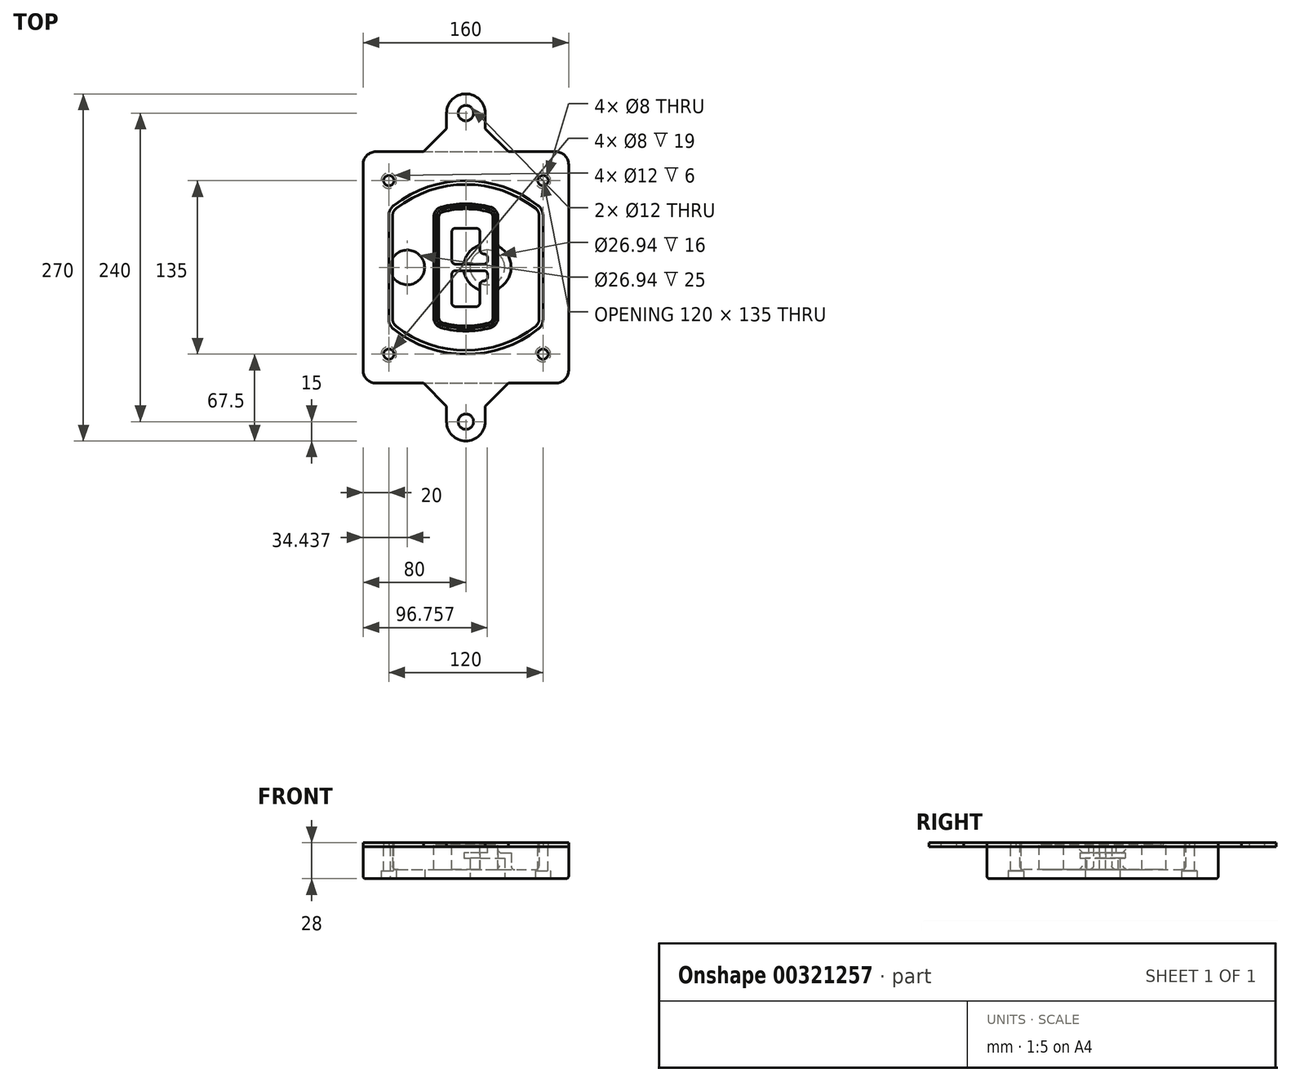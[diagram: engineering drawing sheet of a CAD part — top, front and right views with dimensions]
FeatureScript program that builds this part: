
annotation { "Feature Type Name" : "Feature", "Feature Type Description" : "" }
export const myFeature = defineFeature(function(context is Context, id is Id, definition is map)
    precondition{}
    {
        {
            var Q0;
            Q0=qCreatedBy(makeId("Top.planeOp"),FACE);
            var sketch = newSketch(context, id + "F0", { "sketchPlane" : qUnion([Q0])});
            skPoint(sketch, "E0.rect.middle", {"position": v(0, 0) * mm});
            skLineSegment(sketch, "E1.bottom", {"start": v(-70, -90) * mm, "end": v(70, -90) * mm});
            skLineSegment(sketch, "E1.top", {"start": v(-70, 90) * mm, "end": v(70, 90) * mm});
            skLineSegment(sketch, "E1.left", {"start": v(-80, -80) * mm, "end": v(-80, 80) * mm});
            skLineSegment(sketch, "E1.right", {"start": v(80, -80) * mm, "end": v(80, 80) * mm});
            skLineSegment(sketch, "E2", {"start": v(-80, 90) * mm, "end": v(80, -90) * mm, "construction": true});
            skLineSegment(sketch, "E3", {"start": v(80, 90) * mm, "end": v(-80, -90) * mm, "construction": true});
            skCircle(sketch, "E4", {"center": v(-60, 67.5) * mm, "radius": 4 * mm});
            skCircle(sketch, "E5", {"center": v(60, 67.5) * mm, "radius": 4 * mm});
            skCircle(sketch, "E6", {"center": v(60, -67.5) * mm, "radius": 4 * mm});
            skCircle(sketch, "E7", {"center": v(-60, -67.5) * mm, "radius": 4 * mm});
            skLineSegment(sketch, "E8", {"start": v(-60, 67.5) * mm, "end": v(60, 67.5) * mm, "construction": true});
            skLineSegment(sketch, "E9", {"start": v(60, 67.5) * mm, "end": v(60, -67.5) * mm, "construction": true});
            skLineSegment(sketch, "E10", {"start": v(60, -67.5) * mm, "end": v(-60, -67.5) * mm, "construction": true});
            skLineSegment(sketch, "E11", {"start": v(-60, -67.5) * mm, "end": v(-60, 67.5) * mm, "construction": true});
            skLineSegment(sketch, "E12", {"start": v(-60, 40.3) * mm, "end": v(-60, -40.3) * mm});
            skLineSegment(sketch, "E13", {"start": v(60, 40.3) * mm, "end": v(60, -40.3) * mm});
            skArc(sketch, "E14", {"start": v(56.15, 48.18) * mm, "mid": v(0, 67.5) * mm, "end": v(-56.15, 48.18) * mm});
            skArc(sketch, "E15", {"start": v(-56.15, -48.18) * mm, "mid": v(0, -67.5) * mm, "end": v(56.15, -48.18) * mm});
            skLineSegment(sketch, "E16", {"start": v(-60, 0) * mm, "end": v(60, 0) * mm, "construction": true});
            skPoint(sketch, "E17.visualSharp", {"position": v(-60, -45) * mm});
            skArc(sketch, "E17.filletArc", {"start": v(-60, -40.3) * mm, "mid": v(-58.99, -44.68) * mm, "end": v(-56.15, -48.18) * mm});
            skPoint(sketch, "E18.visualSharp", {"position": v(-60, 45) * mm});
            skArc(sketch, "E18.filletArc", {"start": v(-56.15, 48.18) * mm, "mid": v(-58.99, 44.68) * mm, "end": v(-60, 40.3) * mm});
            skPoint(sketch, "E19.visualSharp", {"position": v(60, 45) * mm});
            skArc(sketch, "E19.filletArc", {"start": v(60, 40.3) * mm, "mid": v(58.99, 44.68) * mm, "end": v(56.15, 48.18) * mm});
            skPoint(sketch, "E20.visualSharp", {"position": v(60, -45) * mm});
            skArc(sketch, "E20.filletArc", {"start": v(56.15, -48.18) * mm, "mid": v(58.99, -44.68) * mm, "end": v(60, -40.3) * mm});
            skPoint(sketch, "E21.visualSharp", {"position": v(-80, 90) * mm});
            skArc(sketch, "E21.filletArc", {"start": v(-70, 90) * mm, "mid": v(-77.07, 87.07) * mm, "end": v(-80, 80) * mm});
            skPoint(sketch, "E22.visualSharp", {"position": v(80, 90) * mm});
            skArc(sketch, "E22.filletArc", {"start": v(80, 80) * mm, "mid": v(77.07, 87.07) * mm, "end": v(70, 90) * mm});
            skPoint(sketch, "E23.visualSharp", {"position": v(80, -90) * mm});
            skArc(sketch, "E23.filletArc", {"start": v(70, -90) * mm, "mid": v(77.07, -87.07) * mm, "end": v(80, -80) * mm});
            skPoint(sketch, "E24.visualSharp", {"position": v(-80, -90) * mm});
            skArc(sketch, "E24.filletArc", {"start": v(-80, -80) * mm, "mid": v(-77.07, -87.07) * mm, "end": v(-70, -90) * mm});
            skArc(sketch, "E25.0", {"start": v(57, 40.3) * mm, "mid": v(56.3, 43.36) * mm, "end": v(54.3, 45.81) * mm});
            skLineSegment(sketch, "E25.1", {"start": v(57, 40.3) * mm, "end": v(57, -40.3) * mm});
            skArc(sketch, "E25.2", {"start": v(54.3, -45.81) * mm, "mid": v(56.3, -43.36) * mm, "end": v(57, -40.3) * mm});
            skArc(sketch, "E25.3", {"start": v(-54.3, -45.81) * mm, "mid": v(0, -64.5) * mm, "end": v(54.3, -45.81) * mm});
            skArc(sketch, "E25.4", {"start": v(-57, -40.3) * mm, "mid": v(-56.3, -43.36) * mm, "end": v(-54.3, -45.81) * mm});
            skArc(sketch, "E25.5", {"start": v(54.3, 45.81) * mm, "mid": v(0, 64.5) * mm, "end": v(-54.3, 45.81) * mm});
            skLineSegment(sketch, "E25.6", {"start": v(-57, 40.3) * mm, "end": v(-57, -40.3) * mm});
            skArc(sketch, "E25.7", {"start": v(-54.3, 45.81) * mm, "mid": v(-56.3, 43.36) * mm, "end": v(-57, 40.3) * mm});
            skArc(sketch, "E26.0", {"start": v(-58.62, 51.33) * mm, "mid": v(-62.58, 46.43) * mm, "end": v(-64, 40.3) * mm});
            skArc(sketch, "E26.1", {"start": v(58.62, 51.33) * mm, "mid": v(0, 71.5) * mm, "end": v(-58.62, 51.33) * mm});
            skArc(sketch, "E26.2", {"start": v(64, 40.3) * mm, "mid": v(62.58, 46.43) * mm, "end": v(58.62, 51.33) * mm});
            skLineSegment(sketch, "E26.3", {"start": v(64, 40.3) * mm, "end": v(64, -40.3) * mm});
            skArc(sketch, "E26.4", {"start": v(58.62, -51.33) * mm, "mid": v(62.58, -46.43) * mm, "end": v(64, -40.3) * mm});
            skLineSegment(sketch, "E26.5", {"start": v(-64, 40.3) * mm, "end": v(-64, -40.3) * mm});
            skArc(sketch, "E26.6", {"start": v(-58.62, -51.33) * mm, "mid": v(0, -71.5) * mm, "end": v(58.62, -51.33) * mm});
            skArc(sketch, "E26.7", {"start": v(-64, -40.3) * mm, "mid": v(-62.58, -46.43) * mm, "end": v(-58.62, -51.33) * mm});
            skSolve(sketch);
        }
        {
            var Q0;
            Q0=makeQuery(id+"F0.imprint","IMPRINT",FACE,{"disambiguationData":[TD([[makeQuery(id+"F0.imprint","IMPRINT",EDGE,{"derivedFrom":sQuery(id+"F0.wireOp",EDGE,"E1.bottom")}),1.0]])]});
            var Q1;
            Q1=makeQuery(id+"F0.imprint","IMPRINT",FACE,{"disambiguationData":[TD([[makeQuery(id+"F0.imprint","IMPRINT",EDGE,{"derivedFrom":sQuery(id+"F0.wireOp",EDGE,"E12")}),1.0]])]});
            var Q2;
            Q2=makeQuery(id+"F0.imprint","IMPRINT",FACE,{"disambiguationData":[TD([[makeQuery(id+"F0.imprint","IMPRINT",EDGE,{"derivedFrom":sQuery(id+"F0.wireOp",EDGE,"E25.0")}),1.0]])]});
            var Q3;
            Q3=makeQuery(id+"F0.imprint","IMPRINT",FACE,{"disambiguationData":[TD([[makeQuery(id+"F0.imprint","IMPRINT",EDGE,{"derivedFrom":sQuery(id+"F0.wireOp",EDGE,"E12")}),-1.0]])]});
            extrude(context, id + "F1", {"entities" : qUnion([Q0, Q1, Q2, Q3]), "oppositeDirection" : true, "depth" : 25 * mm});
        }
        {
            var Q0;
            Q0=makeQuery(id+"F0.imprint","IMPRINT",FACE,{"disambiguationData":[TD([[makeQuery(id+"F0.imprint","IMPRINT",EDGE,{"derivedFrom":sQuery(id+"F0.wireOp",EDGE,"E12")}),1.0]])]});
            extrude(context, id + "F2", {"entities" : qUnion([Q0]), "operationType" : NewBodyOperationType.ADD, "depth" : 3 * mm});
        }
        {
            var Q0;
            Q0=makeQuery(id+"F0.imprint","IMPRINT",FACE,{"disambiguationData":[TD([[makeQuery(id+"F0.imprint","IMPRINT",EDGE,{"derivedFrom":sQuery(id+"F0.wireOp",EDGE,"E25.0")}),1.0]])]});
            extrude(context, id + "F3", {"entities" : qUnion([Q0]), "operationType" : NewBodyOperationType.REMOVE, "oppositeDirection" : true, "depth" : 18 * mm});
        }
        {
            var Q0;
            Q0=makeQuery(id+"F2.opExtrude","CAP_FACE",FACE,{"disambiguationData":[OSD([sQuery(id+"F0.wireOp",EDGE,"E12"),sQuery(id+"F0.wireOp",EDGE,"E13"),sQuery(id+"F0.wireOp",EDGE,"E14"),sQuery(id+"F0.wireOp",EDGE,"E15"),sQuery(id+"F0.wireOp",EDGE,"E17.filletArc"),sQuery(id+"F0.wireOp",EDGE,"E18.filletArc"),sQuery(id+"F0.wireOp",EDGE,"E19.filletArc"),sQuery(id+"F0.wireOp",EDGE,"E20.filletArc"),sQuery(id+"F0.wireOp",EDGE,"E25.0"),sQuery(id+"F0.wireOp",EDGE,"E25.1"),sQuery(id+"F0.wireOp",EDGE,"E25.2"),sQuery(id+"F0.wireOp",EDGE,"E25.3"),sQuery(id+"F0.wireOp",EDGE,"E25.4"),sQuery(id+"F0.wireOp",EDGE,"E25.5"),sQuery(id+"F0.wireOp",EDGE,"E25.6"),sQuery(id+"F0.wireOp",EDGE,"E25.7")])],"isStart":false});
            var sketch = newSketch(context, id + "F4", { "sketchPlane" : qUnion([Q0])});
            skArc(sketch, "E27.0", {"start": v(-19.08, -46.97) * mm, "mid": v(0, -49.5) * mm, "end": v(19.08, -46.97) * mm});
            skArc(sketch, "E28.0", {"start": v(19.08, 46.97) * mm, "mid": v(0, 49.5) * mm, "end": v(-19.08, 46.97) * mm});
            skLineSegment(sketch, "E29", {"start": v(-25, 39.25) * mm, "end": v(-25, -39.25) * mm});
            skLineSegment(sketch, "E30", {"start": v(25, 39.25) * mm, "end": v(25, -39.25) * mm});
            skLineSegment(sketch, "E31", {"start": v(-25, 45.1) * mm, "end": v(25, 45.1) * mm, "construction": true});
            skLineSegment(sketch, "E32", {"start": v(-25, -45.1) * mm, "end": v(25, -45.1) * mm, "construction": true});
            skPoint(sketch, "E33.visualSharp", {"position": v(-25, 45.1) * mm});
            skArc(sketch, "E33.filletArc", {"start": v(-19.08, 46.97) * mm, "mid": v(-23.35, 44.11) * mm, "end": v(-25, 39.25) * mm});
            skPoint(sketch, "E34.visualSharp", {"position": v(25, 45.1) * mm});
            skArc(sketch, "E34.filletArc", {"start": v(25, 39.25) * mm, "mid": v(23.35, 44.11) * mm, "end": v(19.08, 46.97) * mm});
            skPoint(sketch, "E35.visualSharp", {"position": v(25, -45.1) * mm});
            skArc(sketch, "E35.filletArc", {"start": v(19.08, -46.97) * mm, "mid": v(23.35, -44.11) * mm, "end": v(25, -39.25) * mm});
            skPoint(sketch, "E36.visualSharp", {"position": v(-25, -45.1) * mm});
            skArc(sketch, "E36.filletArc", {"start": v(-25, -39.25) * mm, "mid": v(-23.35, -44.11) * mm, "end": v(-19.08, -46.97) * mm});
            skArc(sketch, "E37.0", {"start": v(54.3, 45.81) * mm, "mid": v(0, 64.5) * mm, "end": v(-54.3, 45.81) * mm});
            skArc(sketch, "E37.1", {"start": v(-54.3, 45.81) * mm, "mid": v(-56.3, 43.36) * mm, "end": v(-57, 40.3) * mm});
            skLineSegment(sketch, "E37.2", {"start": v(-57, 40.3) * mm, "end": v(-57, -40.3) * mm});
            skArc(sketch, "E37.3", {"start": v(-57, -40.3) * mm, "mid": v(-56.3, -43.36) * mm, "end": v(-54.3, -45.81) * mm});
            skArc(sketch, "E37.4", {"start": v(-54.3, -45.81) * mm, "mid": v(0, -64.5) * mm, "end": v(54.3, -45.81) * mm});
            skArc(sketch, "E37.5", {"start": v(54.3, -45.81) * mm, "mid": v(56.3, -43.36) * mm, "end": v(57, -40.3) * mm});
            skLineSegment(sketch, "E37.6", {"start": v(57, 40.3) * mm, "end": v(57, -40.3) * mm});
            skArc(sketch, "E37.7", {"start": v(57, 40.3) * mm, "mid": v(56.3, 43.36) * mm, "end": v(54.3, 45.81) * mm});
            skLineSegment(sketch, "E38.0", {"start": v(23, 39.25) * mm, "end": v(23, -39.25) * mm});
            skArc(sketch, "E38.1", {"start": v(18.56, -45.04) * mm, "mid": v(21.76, -42.9) * mm, "end": v(23, -39.25) * mm});
            skArc(sketch, "E38.2", {"start": v(-18.56, -45.04) * mm, "mid": v(0, -47.5) * mm, "end": v(18.56, -45.04) * mm});
            skArc(sketch, "E38.3", {"start": v(-23, -39.25) * mm, "mid": v(-21.76, -42.9) * mm, "end": v(-18.56, -45.04) * mm});
            skLineSegment(sketch, "E38.4", {"start": v(-23, 39.25) * mm, "end": v(-23, -39.25) * mm});
            skArc(sketch, "E38.5", {"start": v(23, 39.25) * mm, "mid": v(21.76, 42.9) * mm, "end": v(18.56, 45.04) * mm});
            skArc(sketch, "E38.6", {"start": v(-18.56, 45.04) * mm, "mid": v(-21.76, 42.9) * mm, "end": v(-23, 39.25) * mm});
            skArc(sketch, "E38.7", {"start": v(18.56, 45.04) * mm, "mid": v(0, 47.5) * mm, "end": v(-18.56, 45.04) * mm});
            skArc(sketch, "E39.0", {"start": v(21, 39.25) * mm, "mid": v(20.18, 41.68) * mm, "end": v(18.04, 43.1) * mm});
            skLineSegment(sketch, "E39.1", {"start": v(21, 39.25) * mm, "end": v(21, -39.25) * mm});
            skArc(sketch, "E39.2", {"start": v(18.04, -43.1) * mm, "mid": v(20.18, -41.68) * mm, "end": v(21, -39.25) * mm});
            skArc(sketch, "E39.3", {"start": v(-18.04, -43.1) * mm, "mid": v(0, -45.5) * mm, "end": v(18.04, -43.1) * mm});
            skArc(sketch, "E39.4", {"start": v(-21, -39.25) * mm, "mid": v(-20.18, -41.68) * mm, "end": v(-18.04, -43.1) * mm});
            skArc(sketch, "E39.5", {"start": v(18.04, 43.1) * mm, "mid": v(0, 45.5) * mm, "end": v(-18.04, 43.1) * mm});
            skLineSegment(sketch, "E39.6", {"start": v(-21, 39.25) * mm, "end": v(-21, -39.25) * mm});
            skArc(sketch, "E39.7", {"start": v(-18.04, 43.1) * mm, "mid": v(-20.18, 41.68) * mm, "end": v(-21, 39.25) * mm});
            skLineSegment(sketch, "E40", {"start": v(-25, 0) * mm, "end": v(25, 0) * mm, "construction": true});
            skLineSegment(sketch, "E41", {"start": v(-11, 5.5) * mm, "end": v(-11, 27.5) * mm});
            skLineSegment(sketch, "E42", {"start": v(-8, 30.5) * mm, "end": v(8, 30.5) * mm});
            skLineSegment(sketch, "E43", {"start": v(11, 27.5) * mm, "end": v(11, 13.5) * mm});
            skLineSegment(sketch, "E44", {"start": v(14, 10.5) * mm, "end": v(14, 10.5) * mm});
            skLineSegment(sketch, "E45", {"start": v(17, 7.5) * mm, "end": v(17, 5.5) * mm});
            skLineSegment(sketch, "E46", {"start": v(14, 2.5) * mm, "end": v(-8, 2.5) * mm});
            skPoint(sketch, "E47.visualSharp", {"position": v(-11, 30.5) * mm});
            skArc(sketch, "E47.filletArc", {"start": v(-8, 30.5) * mm, "mid": v(-10.12, 29.62) * mm, "end": v(-11, 27.5) * mm});
            skPoint(sketch, "E48.visualSharp", {"position": v(11, 30.5) * mm});
            skArc(sketch, "E48.filletArc", {"start": v(11, 27.5) * mm, "mid": v(10.12, 29.62) * mm, "end": v(8, 30.5) * mm});
            skPoint(sketch, "E49.visualSharp", {"position": v(11, 10.5) * mm});
            skArc(sketch, "E49.filletArc", {"start": v(11, 13.5) * mm, "mid": v(11.88, 11.38) * mm, "end": v(14, 10.5) * mm});
            skPoint(sketch, "E50.visualSharp", {"position": v(17, 10.5) * mm});
            skArc(sketch, "E50.filletArc", {"start": v(17, 7.5) * mm, "mid": v(16.12, 9.62) * mm, "end": v(14, 10.5) * mm});
            skPoint(sketch, "E51.visualSharp", {"position": v(17, 2.5) * mm});
            skArc(sketch, "E51.filletArc", {"start": v(14, 2.5) * mm, "mid": v(16.12, 3.38) * mm, "end": v(17, 5.5) * mm});
            skPoint(sketch, "E52.visualSharp", {"position": v(-11, 2.5) * mm});
            skArc(sketch, "E52.filletArc", {"start": v(-11, 5.5) * mm, "mid": v(-10.12, 3.38) * mm, "end": v(-8, 2.5) * mm});
            skLineSegment(sketch, "E53.0.MirrorCS", {"start": v(14, -2.5) * mm, "end": v(-8, -2.5) * mm});
            skArc(sketch, "E54.0.MirrorCS", {"start": v(-11, -5.5) * mm, "mid": v(-10.12, -3.38) * mm, "end": v(-8, -2.5) * mm});
            skLineSegment(sketch, "E55.0.MirrorCS", {"start": v(-11, -5.5) * mm, "end": v(-11, -27.5) * mm});
            skArc(sketch, "E56.0.MirrorCS", {"start": v(-8, -30.5) * mm, "mid": v(-10.12, -29.62) * mm, "end": v(-11, -27.5) * mm});
            skLineSegment(sketch, "E57.0.MirrorCS", {"start": v(-8, -30.5) * mm, "end": v(8, -30.5) * mm});
            skArc(sketch, "E58.0.MirrorCS", {"start": v(11, -27.5) * mm, "mid": v(10.12, -29.62) * mm, "end": v(8, -30.5) * mm});
            skLineSegment(sketch, "E59.0.MirrorCS", {"start": v(11, -27.5) * mm, "end": v(11, -13.5) * mm});
            skArc(sketch, "E60.0.MirrorCS", {"start": v(11, -13.5) * mm, "mid": v(11.88, -11.38) * mm, "end": v(14, -10.5) * mm});
            skArc(sketch, "E61.0.MirrorCS", {"start": v(17, -7.5) * mm, "mid": v(16.12, -9.62) * mm, "end": v(14, -10.5) * mm});
            skLineSegment(sketch, "E62.0.MirrorCS", {"start": v(17, -7.5) * mm, "end": v(17, -5.5) * mm});
            skArc(sketch, "E63.0.MirrorCS", {"start": v(14, -2.5) * mm, "mid": v(16.12, -3.38) * mm, "end": v(17, -5.5) * mm});
            skSolve(sketch);
        }
        {
            var Q0;
            Q0=makeQuery(id+"F4.imprint","IMPRINT",FACE,{"disambiguationData":[TD([[makeQuery(id+"F4.imprint","IMPRINT",EDGE,{"derivedFrom":sQuery(id+"F4.wireOp",EDGE,"E27.0")}),1.0]])]});
            var Q1;
            Q1=makeQuery(id+"F4.imprint","IMPRINT",FACE,{"disambiguationData":[TD([[makeQuery(id+"F4.imprint","IMPRINT",EDGE,{"derivedFrom":sQuery(id+"F4.wireOp",EDGE,"E38.0")}),-1.0]])]});
            var Q2;
            Q2=makeQuery(id+"F4.imprint","IMPRINT",FACE,{"disambiguationData":[TD([[makeQuery(id+"F4.imprint","IMPRINT",EDGE,{"derivedFrom":sQuery(id+"F4.wireOp",EDGE,"E39.0")}),1.0]])]});
            extrude(context, id + "F5", {"entities" : qUnion([Q0, Q1, Q2]), "operationType" : NewBodyOperationType.ADD, "endBound" : BoundingType.UP_TO_NEXT, "oppositeDirection" : true, "depth" : 25 * mm});
        }
        {
            var Q0;
            Q0=makeQuery(id+"F4.imprint","IMPRINT",FACE,{"disambiguationData":[TD([[makeQuery(id+"F4.imprint","IMPRINT",EDGE,{"derivedFrom":sQuery(id+"F4.wireOp",EDGE,"E38.0")}),-1.0]])]});
            extrude(context, id + "F6", {"entities" : qUnion([Q0]), "operationType" : NewBodyOperationType.REMOVE, "oppositeDirection" : true, "depth" : 2 * mm});
        }
        {
            var Q0;
            Q0=makeQuery(id+"F1.opExtrude","CAP_FACE",FACE,{"disambiguationData":[OSD([sQuery(id+"F0.wireOp",EDGE,"E1.bottom"),sQuery(id+"F0.wireOp",EDGE,"E1.top"),sQuery(id+"F0.wireOp",EDGE,"E1.left"),sQuery(id+"F0.wireOp",EDGE,"E1.right"),sQuery(id+"F0.wireOp",EDGE,"E4"),sQuery(id+"F0.wireOp",EDGE,"E5"),sQuery(id+"F0.wireOp",EDGE,"E6"),sQuery(id+"F0.wireOp",EDGE,"E7"),sQuery(id+"F0.wireOp",EDGE,"E21.filletArc"),sQuery(id+"F0.wireOp",EDGE,"E22.filletArc"),sQuery(id+"F0.wireOp",EDGE,"E23.filletArc"),sQuery(id+"F0.wireOp",EDGE,"E24.filletArc")])],"isStart":false});
            var sketch = newSketch(context, id + "F7", { "sketchPlane" : qUnion([Q0])});
            skCircle(sketch, "E64", {"center": v(16.76, 0) * mm, "radius": 13.47 * mm});
            skCircle(sketch, "E65", {"center": v(-45.56, 0) * mm, "radius": 13.47 * mm});
            skLineSegment(sketch, "E66", {"start": v(80, 0) * mm, "end": v(-80, 0) * mm});
            skCircle(sketch, "E67", {"center": v(16.76, 0) * mm, "radius": 18.47 * mm});
            skCircle(sketch, "E68", {"center": v(60, -67.5) * mm, "radius": 6 * mm});
            skCircle(sketch, "E69", {"center": v(-60, -67.5) * mm, "radius": 6 * mm});
            skCircle(sketch, "E70", {"center": v(-60, 67.5) * mm, "radius": 6 * mm});
            skCircle(sketch, "E71", {"center": v(60, 67.5) * mm, "radius": 6 * mm});
            skSolve(sketch);
        }
        {
            var Q0;
            {var subQ1=sQuery(id+"F7.wireOp",EDGE,"E66");var subQ4=sQuery(id+"F7.wireOp",EDGE,"E64");var subQ6=makeQuery(id+"F7.imprint","INTERSECT",VERTEX,{"disambiguationData":[OD(0.0)],"derivedFrom":[subQ4,subQ1]});Q0=makeQuery(id+"F7.imprint","IMPRINT",FACE,{"disambiguationData":[TD([[makeQuery(id+"F7.imprint","IMPRINT",EDGE,{"disambiguationData":[TD([[subQ6,-1.0]])],"derivedFrom":subQ4}),-1.0]])]});}
            var Q1;
            {var subQ0=sQuery(id+"F7.wireOp",EDGE,"E66");var subQ1=sQuery(id+"F7.wireOp",EDGE,"E64");var subQ3=makeQuery(id+"F7.imprint","INTERSECT",VERTEX,{"disambiguationData":[OD(0.0)],"derivedFrom":[subQ1,subQ0]});Q1=makeQuery(id+"F7.imprint","IMPRINT",FACE,{"disambiguationData":[TD([[makeQuery(id+"F7.imprint","IMPRINT",EDGE,{"disambiguationData":[TD([[subQ3,-1.0]])],"derivedFrom":subQ1}),1.0]])]});}
            var Q2;
            {var subQ0=sQuery(id+"F7.wireOp",EDGE,"E66");var subQ1=sQuery(id+"F7.wireOp",EDGE,"E64");var subQ3=makeQuery(id+"F7.imprint","INTERSECT",VERTEX,{"disambiguationData":[OD(0.0)],"derivedFrom":[subQ1,subQ0]});Q2=makeQuery(id+"F7.imprint","IMPRINT",FACE,{"disambiguationData":[TD([[makeQuery(id+"F7.imprint","IMPRINT",EDGE,{"disambiguationData":[TD([[subQ3,1.0]])],"derivedFrom":subQ1}),1.0]])]});}
            var Q3;
            {var subQ1=sQuery(id+"F7.wireOp",EDGE,"E66");var subQ4=sQuery(id+"F7.wireOp",EDGE,"E64");var subQ6=makeQuery(id+"F7.imprint","INTERSECT",VERTEX,{"disambiguationData":[OD(0.0)],"derivedFrom":[subQ4,subQ1]});Q3=makeQuery(id+"F7.imprint","IMPRINT",FACE,{"disambiguationData":[TD([[makeQuery(id+"F7.imprint","IMPRINT",EDGE,{"disambiguationData":[TD([[subQ6,1.0]])],"derivedFrom":subQ4}),-1.0]])]});}
            extrude(context, id + "F8", {"entities" : qUnion([Q0, Q1, Q2, Q3]), "operationType" : NewBodyOperationType.ADD, "oppositeDirection" : true, "depth" : 20 * mm});
        }
        {
            var Q0;
            {var subQ0=sQuery(id+"F7.wireOp",EDGE,"E66");var subQ1=sQuery(id+"F7.wireOp",EDGE,"E64");var subQ3=makeQuery(id+"F7.imprint","INTERSECT",VERTEX,{"disambiguationData":[OD(0.0)],"derivedFrom":[subQ1,subQ0]});Q0=makeQuery(id+"F7.imprint","IMPRINT",FACE,{"disambiguationData":[TD([[makeQuery(id+"F7.imprint","IMPRINT",EDGE,{"disambiguationData":[TD([[subQ3,-1.0]])],"derivedFrom":subQ1}),1.0]])]});}
            var Q1;
            {var subQ0=sQuery(id+"F7.wireOp",EDGE,"E66");var subQ1=sQuery(id+"F7.wireOp",EDGE,"E64");var subQ3=makeQuery(id+"F7.imprint","INTERSECT",VERTEX,{"disambiguationData":[OD(0.0)],"derivedFrom":[subQ1,subQ0]});Q1=makeQuery(id+"F7.imprint","IMPRINT",FACE,{"disambiguationData":[TD([[makeQuery(id+"F7.imprint","IMPRINT",EDGE,{"disambiguationData":[TD([[subQ3,1.0]])],"derivedFrom":subQ1}),1.0]])]});}
            extrude(context, id + "F9", {"entities" : qUnion([Q0, Q1]), "operationType" : NewBodyOperationType.REMOVE, "oppositeDirection" : true, "depth" : 16 * mm});
        }
        {
            var Q0;
            {var subQ0=sQuery(id+"F7.wireOp",EDGE,"E66");var subQ1=sQuery(id+"F7.wireOp",EDGE,"E65");var subQ3=makeQuery(id+"F7.imprint","INTERSECT",VERTEX,{"disambiguationData":[OD(0.0)],"derivedFrom":[subQ1,subQ0]});Q0=makeQuery(id+"F7.imprint","IMPRINT",FACE,{"disambiguationData":[TD([[makeQuery(id+"F7.imprint","IMPRINT",EDGE,{"disambiguationData":[TD([[subQ3,-1.0]])],"derivedFrom":subQ1}),1.0]])]});}
            var Q1;
            {var subQ0=sQuery(id+"F7.wireOp",EDGE,"E66");var subQ1=sQuery(id+"F7.wireOp",EDGE,"E65");var subQ3=makeQuery(id+"F7.imprint","INTERSECT",VERTEX,{"disambiguationData":[OD(0.0)],"derivedFrom":[subQ1,subQ0]});Q1=makeQuery(id+"F7.imprint","IMPRINT",FACE,{"disambiguationData":[TD([[makeQuery(id+"F7.imprint","IMPRINT",EDGE,{"disambiguationData":[TD([[subQ3,1.0]])],"derivedFrom":subQ1}),1.0]])]});}
            extrude(context, id + "F10", {"entities" : qUnion([Q0, Q1]), "operationType" : NewBodyOperationType.REMOVE, "oppositeDirection" : true, "depth" : 25 * mm});
        }
        {
            var Q0;
            Q0=makeQuery(id+"F7.imprint","IMPRINT",FACE,{"disambiguationData":[TD([[makeQuery(id+"F7.imprint","IMPRINT",EDGE,{"derivedFrom":sQuery(id+"F7.wireOp",EDGE,"E68")}),1.0]])]});
            var Q1;
            Q1=makeQuery(id+"F7.imprint","IMPRINT",FACE,{"disambiguationData":[TD([[makeQuery(id+"F7.imprint","IMPRINT",EDGE,{"derivedFrom":makeQuery(id+"F1.opExtrude","CAP_EDGE",EDGE,{"disambiguationData":[OSD([sQuery(id+"F0.wireOp",EDGE,"E5")])],"isStart":false})}),-1.0]])]});
            var Q2;
            Q2=makeQuery(id+"F7.imprint","IMPRINT",FACE,{"disambiguationData":[TD([[makeQuery(id+"F7.imprint","IMPRINT",EDGE,{"derivedFrom":sQuery(id+"F7.wireOp",EDGE,"E69")}),1.0]])]});
            var Q3;
            Q3=makeQuery(id+"F7.imprint","IMPRINT",FACE,{"disambiguationData":[TD([[makeQuery(id+"F7.imprint","IMPRINT",EDGE,{"derivedFrom":makeQuery(id+"F1.opExtrude","CAP_EDGE",EDGE,{"disambiguationData":[OSD([sQuery(id+"F0.wireOp",EDGE,"E4")])],"isStart":false})}),-1.0]])]});
            var Q4;
            Q4=makeQuery(id+"F7.imprint","IMPRINT",FACE,{"disambiguationData":[TD([[makeQuery(id+"F7.imprint","IMPRINT",EDGE,{"derivedFrom":sQuery(id+"F7.wireOp",EDGE,"E70")}),1.0]])]});
            var Q5;
            Q5=makeQuery(id+"F7.imprint","IMPRINT",FACE,{"disambiguationData":[TD([[makeQuery(id+"F7.imprint","IMPRINT",EDGE,{"derivedFrom":makeQuery(id+"F1.opExtrude","CAP_EDGE",EDGE,{"disambiguationData":[OSD([sQuery(id+"F0.wireOp",EDGE,"E7")])],"isStart":false})}),-1.0]])]});
            var Q6;
            Q6=makeQuery(id+"F7.imprint","IMPRINT",FACE,{"disambiguationData":[TD([[makeQuery(id+"F7.imprint","IMPRINT",EDGE,{"derivedFrom":sQuery(id+"F7.wireOp",EDGE,"E71")}),1.0]])]});
            var Q7;
            Q7=makeQuery(id+"F7.imprint","IMPRINT",FACE,{"disambiguationData":[TD([[makeQuery(id+"F7.imprint","IMPRINT",EDGE,{"derivedFrom":makeQuery(id+"F1.opExtrude","CAP_EDGE",EDGE,{"disambiguationData":[OSD([sQuery(id+"F0.wireOp",EDGE,"E6")])],"isStart":false})}),-1.0]])]});
            extrude(context, id + "F11", {"entities" : qUnion([Q0, Q1, Q2, Q3, Q4, Q5, Q6, Q7]), "operationType" : NewBodyOperationType.REMOVE, "oppositeDirection" : true, "depth" : 6 * mm});
        }
        {
            var Q0;
            Q0=makeQuery(id+"F9.boolean.opBoolean","COPY",FACE,{"derivedFrom":makeQuery(id+"F9.opExtrude","CAP_FACE",FACE,{"disambiguationData":[OSD([sQuery(id+"F7.wireOp",EDGE,"E64")])],"isStart":false})});
            var sketch = newSketch(context, id + "F12", { "sketchPlane" : qUnion([Q0])});
            skArc(sketch, "E72.0", {"start": v(11, 17.55) * mm, "mid": v(2.57, 11.82) * mm, "end": v(-1.54, 2.5) * mm});
            skArc(sketch, "E72.1", {"start": v(-1.54, -2.5) * mm, "mid": v(2.57, -11.82) * mm, "end": v(11, -17.55) * mm});
            skLineSegment(sketch, "E73", {"start": v(-1.54, -2.5) * mm, "end": v(14, -2.5) * mm});
            skLineSegment(sketch, "E74.0", {"start": v(14, 2.5) * mm, "end": v(-1.54, 2.5) * mm});
            skArc(sketch, "E74.1", {"start": v(14, 2.5) * mm, "mid": v(16.12, 3.38) * mm, "end": v(17, 5.5) * mm});
            skLineSegment(sketch, "E74.2", {"start": v(17, 7.5) * mm, "end": v(17, 5.5) * mm});
            skArc(sketch, "E74.3", {"start": v(17, 7.5) * mm, "mid": v(16.12, 9.62) * mm, "end": v(14, 10.5) * mm});
            skArc(sketch, "E74.4", {"start": v(11, 13.5) * mm, "mid": v(11.88, 11.38) * mm, "end": v(14, 10.5) * mm});
            skLineSegment(sketch, "E74.5", {"start": v(11, 17.55) * mm, "end": v(11, 13.5) * mm});
            skLineSegment(sketch, "E74.7", {"start": v(14, -2.5) * mm, "end": v(-1.54, -2.5) * mm});
            skArc(sketch, "E74.8", {"start": v(14, -2.5) * mm, "mid": v(16.12, -3.38) * mm, "end": v(17, -5.5) * mm});
            skLineSegment(sketch, "E74.9", {"start": v(17, -7.5) * mm, "end": v(17, -5.5) * mm});
            skArc(sketch, "E74.10", {"start": v(17, -7.5) * mm, "mid": v(16.12, -9.62) * mm, "end": v(14, -10.5) * mm});
            skArc(sketch, "E74.11", {"start": v(11, -13.5) * mm, "mid": v(11.88, -11.38) * mm, "end": v(14, -10.5) * mm});
            skLineSegment(sketch, "E74.12", {"start": v(11, -17.55) * mm, "end": v(11, -13.5) * mm});
            skPoint(sketch, "E75.orphan", {"position": v(11, -27.5) * mm});
            skPoint(sketch, "E76.orphan", {"position": v(-8, -2.5) * mm});
            skPoint(sketch, "E77.orphan", {"position": v(-8, 2.5) * mm});
            skPoint(sketch, "E78.orphan", {"position": v(11, 27.5) * mm});
            skSolve(sketch);
        }
        {
            var Q0;
            {var subQ7=sQuery(id+"F12.wireOp",EDGE,"E72.0");var subQ14=sQuery(id+"F12.wireOp",EDGE,"E72.1");var subQ16=sQuery(id+"F12.wireOp",EDGE,"E74.1");var subQ18=sQuery(id+"F12.wireOp",EDGE,"E74.8");Q0=qUnion([makeQuery(id+"F12.imprint","IMPRINT",FACE,{"disambiguationData":[TD([[makeQuery(id+"F12.imprint","IMPRINT",EDGE,{"derivedFrom":subQ7}),1.0]])]}),makeQuery(id+"F12.imprint","IMPRINT",FACE,{"disambiguationData":[TD([[makeQuery(id+"F12.imprint","IMPRINT",EDGE,{"derivedFrom":subQ14}),1.0]])]}),makeQuery(id+"F12.imprint","IMPRINT",FACE,{"disambiguationData":[TD([[makeQuery(id+"F12.imprint","IMPRINT",EDGE,{"derivedFrom":subQ16}),1.0]])]}),makeQuery(id+"F12.imprint","IMPRINT",FACE,{"disambiguationData":[TD([[makeQuery(id+"F12.imprint","IMPRINT",EDGE,{"derivedFrom":subQ18}),-1.0]])]})]);}
            var Q1;
            Q1=makeQuery(id+"F5.boolean.opBoolean","SPLIT",FACE,{"disambiguationData":[TD([makeQuery(id+"F5.opExtrude","SWEPT_FACE",FACE,{"disambiguationData":[OSD([sQuery(id+"F4.wireOp",EDGE,"E41")])]})])],"derivedFrom":makeQuery(id+"F3.boolean.opBoolean","COPY",FACE,{"derivedFrom":makeQuery(id+"F3.opExtrude","CAP_FACE",FACE,{"disambiguationData":[OSD([sQuery(id+"F0.wireOp",EDGE,"E25.0"),sQuery(id+"F0.wireOp",EDGE,"E25.1"),sQuery(id+"F0.wireOp",EDGE,"E25.2"),sQuery(id+"F0.wireOp",EDGE,"E25.3"),sQuery(id+"F0.wireOp",EDGE,"E25.4"),sQuery(id+"F0.wireOp",EDGE,"E25.5"),sQuery(id+"F0.wireOp",EDGE,"E25.6"),sQuery(id+"F0.wireOp",EDGE,"E25.7")])],"isStart":false})})});
            extrude(context, id + "F13", {"entities" : qUnion([Q0]), "operationType" : NewBodyOperationType.REMOVE, "endBound" : BoundingType.UP_TO_SURFACE, "endBoundEntityFace" : qUnion([Q1]), "depth" : 25 * mm});
        }
        {
            var Q0;
            Q0=makeQuery(id+"F3.boolean.opBoolean","COPY",EDGE,{"derivedFrom":makeQuery(id+"F3.opExtrude","CAP_EDGE",EDGE,{"disambiguationData":[OSD([sQuery(id+"F0.wireOp",EDGE,"E25.6")])],"isStart":false})});
            var Q1;
            Q1=makeQuery(id+"F8.boolean.opBoolean","INTERSECT",EDGE,{"derivedFrom":[makeQuery(id+"F5.opExtrude","SWEPT_FACE",FACE,{"disambiguationData":[OSD([sQuery(id+"F4.wireOp",EDGE,"E30")])]}),makeQuery(id+"F8.opExtrude","CAP_FACE",FACE,{"disambiguationData":[OSD([sQuery(id+"F7.wireOp",EDGE,"E67")])],"isStart":false})]});
            var Q2;
            Q2=makeQuery(id+"F8.boolean.opBoolean","INTERSECT",EDGE,{"disambiguationData":[OD(1.0)],"derivedFrom":[makeQuery(id+"F5.opExtrude","SWEPT_FACE",FACE,{"disambiguationData":[OSD([sQuery(id+"F4.wireOp",EDGE,"E30")])]}),makeQuery(id+"F8.opExtrude","SWEPT_FACE",FACE,{"disambiguationData":[OSD([sQuery(id+"F7.wireOp",EDGE,"E67")])]})]});
            var Q3;
            {var subQ0=sQuery(id+"F4.wireOp",EDGE,"E30");Q3=makeQuery(id+"F8.boolean.opBoolean","SPLIT",EDGE,{"disambiguationData":[TD([makeQuery(id+"F5.opExtrude","SWEPT_FACE",FACE,{"disambiguationData":[OSD([sQuery(id+"F4.wireOp",EDGE,"E35.filletArc")])]})])],"derivedFrom":makeQuery(id+"F5.opExtrude","CAP_EDGE",EDGE,{"disambiguationData":[OSD([subQ0])],"isStart":false})});}
            var Q4;
            {var subQ0=sQuery(id+"F0.wireOp",EDGE,"E25.7");var subQ1=sQuery(id+"F0.wireOp",EDGE,"E25.1");var subQ2=sQuery(id+"F0.wireOp",EDGE,"E25.6");var subQ3=sQuery(id+"F0.wireOp",EDGE,"E25.5");var subQ4=sQuery(id+"F0.wireOp",EDGE,"E25.4");var subQ5=sQuery(id+"F0.wireOp",EDGE,"E25.0");var subQ6=sQuery(id+"F0.wireOp",EDGE,"E25.2");var subQ7=sQuery(id+"F0.wireOp",EDGE,"E25.3");Q4=makeQuery(id+"F8.boolean.opBoolean","INTERSECT",EDGE,{"derivedFrom":[makeQuery(id+"F5.boolean.opBoolean","SPLIT",FACE,{"disambiguationData":[TD([makeQuery(id+"F2.opExtrude","SWEPT_FACE",FACE,{"disambiguationData":[OSD([subQ5])]})])],"derivedFrom":makeQuery(id+"F3.boolean.opBoolean","COPY",FACE,{"derivedFrom":makeQuery(id+"F3.opExtrude","CAP_FACE",FACE,{"disambiguationData":[OSD([subQ5,subQ1,subQ6,subQ7,subQ4,subQ3,subQ2,subQ0])],"isStart":false})})}),makeQuery(id+"F8.opExtrude","SWEPT_FACE",FACE,{"disambiguationData":[OSD([sQuery(id+"F7.wireOp",EDGE,"E67")])]})]});}
            var Q5;
            Q5=makeQuery(id+"F8.boolean.opBoolean","INTERSECT",EDGE,{"disambiguationData":[OD(0.0)],"derivedFrom":[makeQuery(id+"F5.opExtrude","SWEPT_FACE",FACE,{"disambiguationData":[OSD([sQuery(id+"F4.wireOp",EDGE,"E30")])]}),makeQuery(id+"F8.opExtrude","SWEPT_FACE",FACE,{"disambiguationData":[OSD([sQuery(id+"F7.wireOp",EDGE,"E67")])]})]});
            fillet(context, id + "F14", {"entities" : qUnion([Q0, Q1, Q2, Q3, Q4, Q5]), "radius" : 3 * mm, "tangentPropagation" : true, "allowEdgeOverflow" : false});
        }
        {
            var Q0;
            Q0=makeQuery(id+"F1.opExtrude","CAP_EDGE",EDGE,{"disambiguationData":[OSD([sQuery(id+"F0.wireOp",EDGE,"E1.bottom")])],"isStart":false});
            fillet(context, id + "F15", {"entities" : qUnion([Q0]), "radius" : 2 * mm, "tangentPropagation" : true, "allowEdgeOverflow" : false});
        }
        {
            var Q0;
            {var subQ0=sQuery(id+"F0.wireOp",EDGE,"E21.filletArc");var subQ1=sQuery(id+"F0.wireOp",EDGE,"E7");var subQ2=sQuery(id+"F0.wireOp",EDGE,"E6");var subQ3=sQuery(id+"F0.wireOp",EDGE,"E5");var subQ4=sQuery(id+"F0.wireOp",EDGE,"E4");var subQ5=sQuery(id+"F0.wireOp",EDGE,"E22.filletArc");var subQ6=sQuery(id+"F0.wireOp",EDGE,"E1.bottom");var subQ7=sQuery(id+"F0.wireOp",EDGE,"E1.right");var subQ8=sQuery(id+"F0.wireOp",EDGE,"E1.top");var subQ9=sQuery(id+"F0.wireOp",EDGE,"E1.left");var subQ10=sQuery(id+"F0.wireOp",EDGE,"E23.filletArc");var subQ11=sQuery(id+"F0.wireOp",EDGE,"E24.filletArc");Q0=makeQuery(id+"F2.boolean.opBoolean","SPLIT",FACE,{"disambiguationData":[TD([makeQuery(id+"F1.opExtrude","SWEPT_FACE",FACE,{"disambiguationData":[OSD([subQ6])]})])],"derivedFrom":makeQuery(id+"F1.opExtrude","CAP_FACE",FACE,{"disambiguationData":[OSD([subQ6,subQ8,subQ9,subQ7,subQ4,subQ3,subQ2,subQ1,subQ0,subQ5,subQ10,subQ11])],"isStart":true})});}
            var sketch = newSketch(context, id + "F16", { "sketchPlane" : qUnion([Q0])});
            skLineSegment(sketch, "E79", {"start": v(0, 90) * mm, "end": v(0, 120) * mm});
            skPoint(sketch, "E79.endSnap0", {"position": v(0, 90) * mm});
            skCircle(sketch, "E80", {"center": v(0, 120) * mm, "radius": 6 * mm});
            skCircle(sketch, "E81", {"center": v(0, 120) * mm, "radius": 15 * mm});
            skLineSegment(sketch, "E82", {"start": v(15, 120) * mm, "end": v(15, 108) * mm});
            skLineSegment(sketch, "E83", {"start": v(-15, 120) * mm, "end": v(-15, 108) * mm});
            skLineSegment(sketch, "E84", {"start": v(-15, 108) * mm, "end": v(-33, 90) * mm});
            skLineSegment(sketch, "E85", {"start": v(15, 108) * mm, "end": v(33, 90) * mm});
            skLineSegment(sketch, "E86", {"start": v(-80, 0) * mm, "end": v(80, 0) * mm});
            skCircle(sketch, "E87.MirrorC", {"center": v(0, -120) * mm, "radius": 6 * mm});
            skCircle(sketch, "E88.MirrorC", {"center": v(0, -120) * mm, "radius": 15 * mm});
            skLineSegment(sketch, "E89.MirrorCS", {"start": v(0, -90) * mm, "end": v(0, -120) * mm});
            skLineSegment(sketch, "E90.MirrorCS", {"start": v(-15, -120) * mm, "end": v(-15, -108) * mm});
            skLineSegment(sketch, "E91.MirrorCS", {"start": v(15, -120) * mm, "end": v(15, -108) * mm});
            skLineSegment(sketch, "E92.MirrorCS", {"start": v(15, -108) * mm, "end": v(33, -90) * mm});
            skLineSegment(sketch, "E93.MirrorCS", {"start": v(-15, -108) * mm, "end": v(-33, -90) * mm});
            skSolve(sketch);
        }
        {
            var Q0;
            Q0=qSketchRegion(id+"F16",true);
            var Q1;
            {var subQ1=sQuery(id+"F16.wireOp",EDGE,"E90.MirrorCS");Q1=makeQuery(id+"F16.imprint","IMPRINT",FACE,{"disambiguationData":[TD([[makeQuery(id+"F16.imprint","IMPRINT",EDGE,{"derivedFrom":subQ1}),-1.0]])]});}
            var Q2;
            {var subQ1=sQuery(id+"F16.wireOp",EDGE,"E91.MirrorCS");Q2=makeQuery(id+"F16.imprint","IMPRINT",FACE,{"disambiguationData":[TD([[makeQuery(id+"F16.imprint","IMPRINT",EDGE,{"derivedFrom":subQ1}),1.0]])]});}
            var Q3;
            {var subQ1=sQuery(id+"F16.wireOp",EDGE,"E83");Q3=makeQuery(id+"F16.imprint","IMPRINT",FACE,{"disambiguationData":[TD([[makeQuery(id+"F16.imprint","IMPRINT",EDGE,{"derivedFrom":subQ1}),1.0]])]});}
            var Q4;
            {var subQ1=sQuery(id+"F16.wireOp",EDGE,"E82");Q4=makeQuery(id+"F16.imprint","IMPRINT",FACE,{"disambiguationData":[TD([[makeQuery(id+"F16.imprint","IMPRINT",EDGE,{"derivedFrom":subQ1}),-1.0]])]});}
            var Q5;
            Q5=makeQuery(id+"F16.imprint","IMPRINT",FACE,{"disambiguationData":[TD([[makeQuery(id+"F16.imprint","IMPRINT",EDGE,{"derivedFrom":makeQuery(id+"F1.opExtrude","CAP_EDGE",EDGE,{"disambiguationData":[OSD([sQuery(id+"F0.wireOp",EDGE,"E6")])],"isStart":true})}),-1.0]])]});
            var Q6;
            Q6=makeQuery(id+"F16.imprint","IMPRINT",FACE,{"disambiguationData":[TD([[makeQuery(id+"F16.imprint","IMPRINT",EDGE,{"derivedFrom":makeQuery(id+"F1.opExtrude","CAP_EDGE",EDGE,{"disambiguationData":[OSD([sQuery(id+"F0.wireOp",EDGE,"E4")])],"isStart":true})}),-1.0]])]});
            var Q7;
            Q7=makeQuery(id+"F2.opExtrude","CAP_FACE",FACE,{"disambiguationData":[OSD([sQuery(id+"F0.wireOp",EDGE,"E12"),sQuery(id+"F0.wireOp",EDGE,"E13"),sQuery(id+"F0.wireOp",EDGE,"E14"),sQuery(id+"F0.wireOp",EDGE,"E15"),sQuery(id+"F0.wireOp",EDGE,"E17.filletArc"),sQuery(id+"F0.wireOp",EDGE,"E18.filletArc"),sQuery(id+"F0.wireOp",EDGE,"E19.filletArc"),sQuery(id+"F0.wireOp",EDGE,"E20.filletArc"),sQuery(id+"F0.wireOp",EDGE,"E25.0"),sQuery(id+"F0.wireOp",EDGE,"E25.1"),sQuery(id+"F0.wireOp",EDGE,"E25.2"),sQuery(id+"F0.wireOp",EDGE,"E25.3"),sQuery(id+"F0.wireOp",EDGE,"E25.4"),sQuery(id+"F0.wireOp",EDGE,"E25.5"),sQuery(id+"F0.wireOp",EDGE,"E25.6"),sQuery(id+"F0.wireOp",EDGE,"E25.7")])],"isStart":false});
            extrude(context, id + "F17", {"entities" : qUnion([Q0, Q1, Q2, Q3, Q4, Q5, Q6]), "endBound" : BoundingType.UP_TO_SURFACE, "endBoundEntityFace" : qUnion([Q7]), "depth" : 25 * mm});
        }
    });
